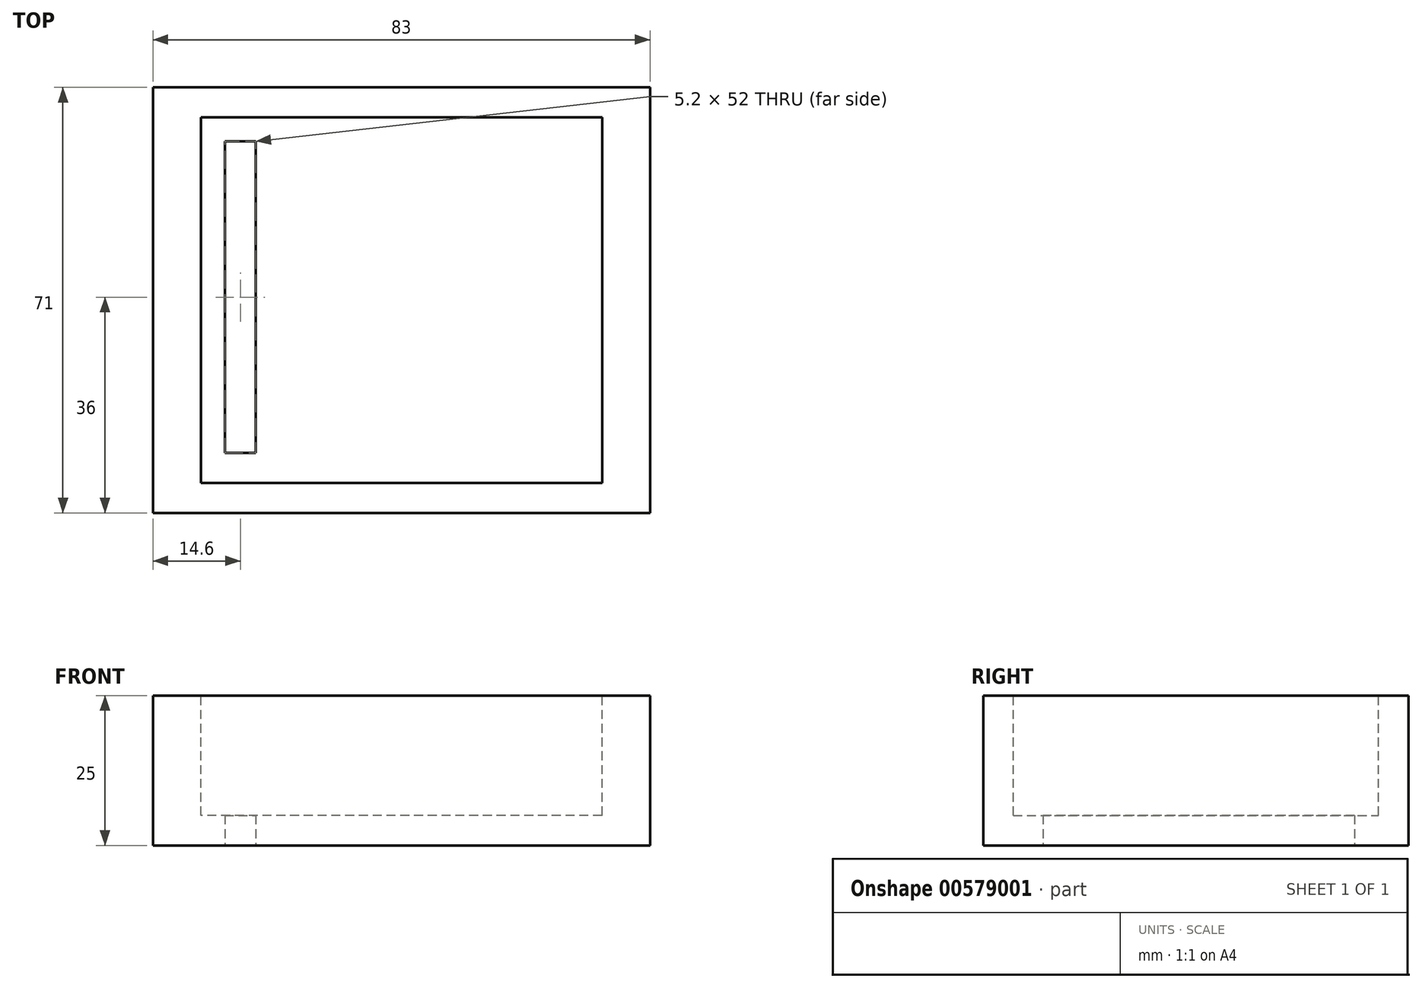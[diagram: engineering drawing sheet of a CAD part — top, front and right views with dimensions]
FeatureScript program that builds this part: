
annotation { "Feature Type Name" : "Feature", "Feature Type Description" : "" }
export const myFeature = defineFeature(function(context is Context, id is Id, definition is map)
    precondition{}
    {
        {
            var Q0;
            Q0=qCreatedBy(makeId("Top.planeOp"),FACE);
            var sketch = newSketch(context, id + "F0", { "sketchPlane" : qUnion([Q0])});
            skLineSegment(sketch, "E0.bottom", {"start": v(41.5, -35.5) * mm, "end": v(-41.5, -35.5) * mm});
            skLineSegment(sketch, "E0.top", {"start": v(41.5, 35.5) * mm, "end": v(-41.5, 35.5) * mm});
            skLineSegment(sketch, "E0.left", {"start": v(41.5, -35.5) * mm, "end": v(41.5, 35.5) * mm});
            skLineSegment(sketch, "E0.right", {"start": v(-41.5, -35.5) * mm, "end": v(-41.5, 35.5) * mm});
            skPoint(sketch, "E0.middle", {"position": v(0, 0) * mm});
            skSolve(sketch);
        }
        {
            var Q0;
            Q0 = qSketchRegion(id + "F0", true);
            extrude(context, id + "F1", {"entities" : qUnion([Q0]), "depth" : 25 * mm, "offsetDistance" : 25 * mm});
        }
        {
            var Q0;
            Q0=makeQuery(id+"F1.opExtrude","CAP_FACE",FACE,{"disambiguationData":[OSD([sQuery(id+"F0.wireOp",EDGE,"E0.bottom"),sQuery(id+"F0.wireOp",EDGE,"E0.top"),sQuery(id+"F0.wireOp",EDGE,"E0.left"),sQuery(id+"F0.wireOp",EDGE,"E0.right")])],"isStart":false});
            var sketch = newSketch(context, id + "F2", { "sketchPlane" : qUnion([Q0])});
            skLineSegment(sketch, "E1.bottom", {"start": v(33.5, -30.5) * mm, "end": v(-33.5, -30.5) * mm});
            skLineSegment(sketch, "E1.top", {"start": v(33.5, 30.5) * mm, "end": v(-33.5, 30.5) * mm});
            skLineSegment(sketch, "E1.left", {"start": v(33.5, -30.5) * mm, "end": v(33.5, 30.5) * mm});
            skLineSegment(sketch, "E1.right", {"start": v(-33.5, -30.5) * mm, "end": v(-33.5, 30.5) * mm});
            skPoint(sketch, "E1.middle", {"position": v(0, 0) * mm});
            skSolve(sketch);
        }
        {
            var Q0;
            Q0 = qSketchRegion(id + "F2", true);
            extrude(context, id + "F3", {"entities" : qUnion([Q0]), "operationType" : NewBodyOperationType.REMOVE, "oppositeDirection" : true, "depth" : 20 * mm, "offsetDistance" : 25 * mm});
        }
        {
            var Q0;
            Q0=qCreatedBy(makeId("Top.planeOp"),FACE);
            var sketch = newSketch(context, id + "F4", { "sketchPlane" : qUnion([Q0])});
            skLineSegment(sketch, "E2.bottom", {"start": v(-24.3, -25.5) * mm, "end": v(-29.5, -25.5) * mm});
            skLineSegment(sketch, "E2.top", {"start": v(-24.3, 26.5) * mm, "end": v(-29.5, 26.5) * mm});
            skLineSegment(sketch, "E2.left", {"start": v(-24.3, -25.5) * mm, "end": v(-24.3, 26.5) * mm});
            skLineSegment(sketch, "E2.right", {"start": v(-29.5, -25.5) * mm, "end": v(-29.5, 26.5) * mm});
            skPoint(sketch, "E2.middle", {"position": v(-26.9, 0.5) * mm});
            skSolve(sketch);
        }
        {
            var Q0;
            Q0 = qSketchRegion(id + "F4", true);
            extrude(context, id + "F5", {"entities" : qUnion([Q0]), "operationType" : NewBodyOperationType.REMOVE, "endBound" : BoundingType.THROUGH_ALL, "depth" : 25 * mm, "offsetDistance" : 25 * mm});
        }
    });
